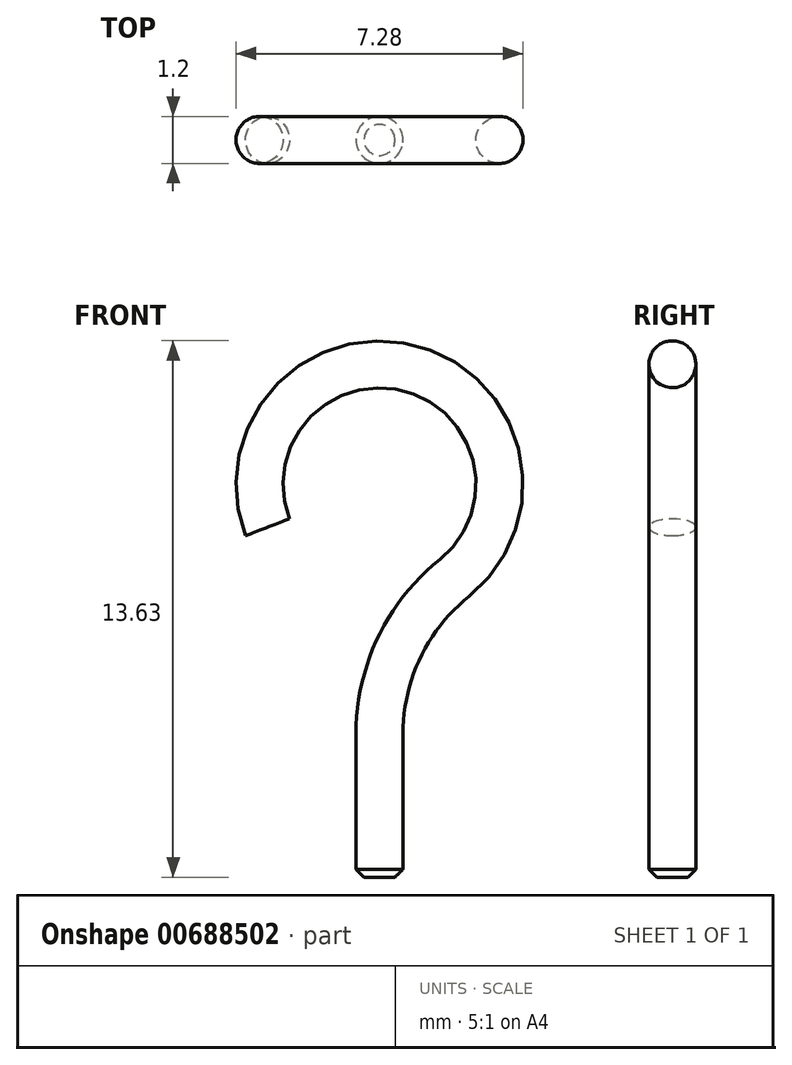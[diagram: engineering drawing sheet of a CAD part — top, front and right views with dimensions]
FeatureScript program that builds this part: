
annotation { "Feature Type Name" : "Feature", "Feature Type Description" : "" }
export const myFeature = defineFeature(function(context is Context, id is Id, definition is map)
    precondition{}
    {
        {
            var Q0;
            Q0=qCreatedBy(makeId("Front.planeOp"),FACE);
            var sketch = newSketch(context, id + "F0", { "sketchPlane" : qUnion([Q0])});
            skArc(sketch, "E0", {"start": v(1.9, 7.6) * mm, "mid": v(0.8, 12.92) * mm, "end": v(-2.85, 8.9) * mm});
            skLineSegment(sketch, "E1", {"start": v(0, 3.64) * mm, "end": v(0, 0) * mm});
            skArc(sketch, "E2.filletArc", {"start": v(1.9, 7.6) * mm, "mid": v(0.5, 5.84) * mm, "end": v(0, 3.64) * mm});
            skSolve(sketch);
        }
        {
            var Q0;
            Q0=qCreatedBy(makeId("Top.planeOp"),FACE);
            var sketch = newSketch(context, id + "F1", { "sketchPlane" : qUnion([Q0])});
            skCircle(sketch, "E3", {"center": v(0, 0) * mm, "radius": 0.6 * mm});
            skSolve(sketch);
        }
        {
            var Q0;
            Q0=makeQuery(id+"F1.imprint","IMPRINT",FACE,{"disambiguationData":[TD([[makeQuery(id+"F1.imprint","IMPRINT",EDGE,{"derivedFrom":sQuery(id+"F1.wireOp",EDGE,"E3")}),1.0]])]});
            var Q1;
            Q1=sQuery(id+"F0.wireOp",EDGE,"E1");
            var Q2;
            Q2=sQuery(id+"F0.wireOp",EDGE,"E2.filletArc");
            var Q3;
            Q3=sQuery(id+"F0.wireOp",EDGE,"E0");
            sweep(context, id + "F2", {"profiles" : qUnion([Q0]), "path" : qUnion([Q1, Q2, Q3])});
        }
        {
            var Q0;
            Q0=makeQuery(id+"F2.opSweep","CAP_EDGE",EDGE,{"disambiguationData":[OSD([sQuery(id+"F0.wireOp",VERTEX,"E1.end"),sQuery(id+"F1.wireOp",EDGE,"E3")])],"isStart":true});
            chamfer(context, id + "F3", {"entities" : qUnion([Q0]), "width" : 0.2 * mm, "tangentPropagation" : true});
        }
    });
